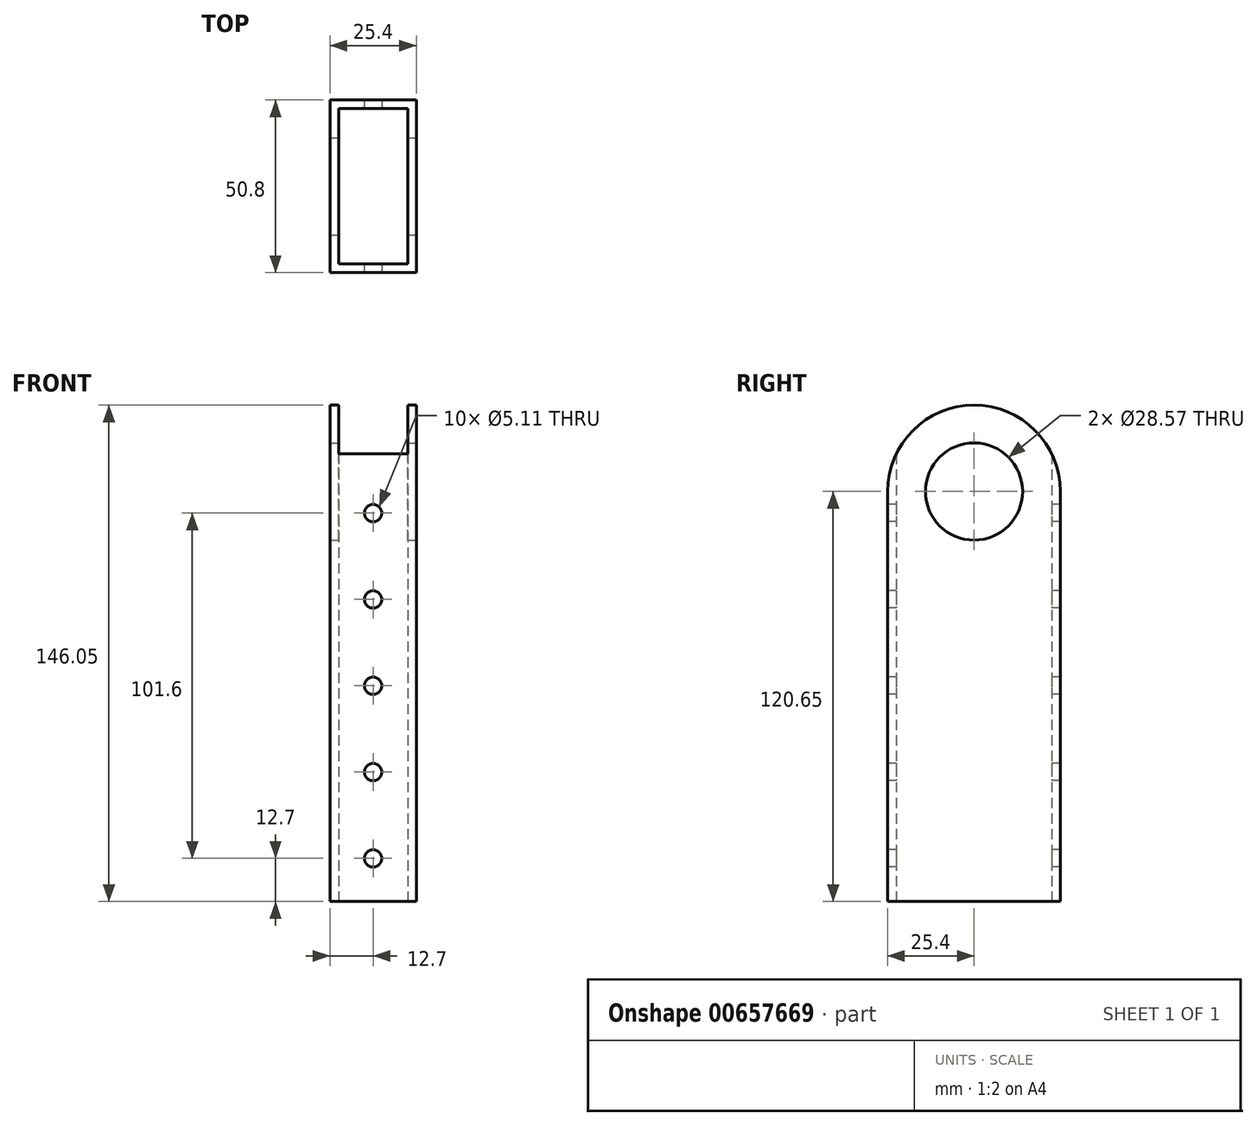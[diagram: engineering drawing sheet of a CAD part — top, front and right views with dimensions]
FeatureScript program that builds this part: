
annotation { "Feature Type Name" : "Feature", "Feature Type Description" : "" }
export const myFeature = defineFeature(function(context is Context, id is Id, definition is map)
    precondition{}
    {
        {
            var Q0;
            Q0=qCreatedBy(makeId("Top.planeOp"),FACE);
            var sketch = newSketch(context, id + "F0", { "sketchPlane" : qUnion([Q0])});
            skLineSegment(sketch, "E0.bottom", {"start": v(0, 0) * mm, "end": v(25.4, 0) * mm});
            skLineSegment(sketch, "E0.top", {"start": v(0, -50.8) * mm, "end": v(25.4, -50.8) * mm});
            skLineSegment(sketch, "E0.left", {"start": v(0, 0) * mm, "end": v(0, -50.8) * mm});
            skLineSegment(sketch, "E0.right", {"start": v(25.4, 0) * mm, "end": v(25.4, -50.8) * mm});
            skLineSegment(sketch, "E1.bottom", {"start": v(2.54, -2.54) * mm, "end": v(22.86, -2.54) * mm});
            skLineSegment(sketch, "E1.top", {"start": v(2.54, -48.26) * mm, "end": v(22.86, -48.26) * mm});
            skLineSegment(sketch, "E1.left", {"start": v(2.54, -2.54) * mm, "end": v(2.54, -48.26) * mm});
            skLineSegment(sketch, "E1.right", {"start": v(22.86, -2.54) * mm, "end": v(22.86, -48.26) * mm});
            skSolve(sketch);
        }
        {
            var Q0;
            Q0=makeQuery(id+"F0.imprint","IMPRINT",FACE,{"disambiguationData":[TD([[makeQuery(id+"F0.imprint","IMPRINT",EDGE,{"derivedFrom":sQuery(id+"F0.wireOp",EDGE,"E0.bottom")}),-1.0]])]});
            extrude(context, id + "F1", {"entities" : qUnion([Q0]), "depth" : 146.05 * mm, "offsetDistance" : 25.4 * mm});
        }
        {
            var Q0;
            Q0=makeQuery(id+"F1.opExtrude","SWEPT_FACE",FACE,{"disambiguationData":[OSD([sQuery(id+"F0.wireOp",EDGE,"E0.top")])]});
            var sketch = newSketch(context, id + "F2", { "sketchPlane" : qUnion([Q0])});
            skCircle(sketch, "E2", {"center": v(12.7, 12.7) * mm, "radius": 2.55 * mm});
            skCircle(sketch, "E3.0.1.0", {"center": v(12.7, 38.1) * mm, "radius": 2.55 * mm});
            skCircle(sketch, "E3.0.2.0", {"center": v(12.7, 63.5) * mm, "radius": 2.55 * mm});
            skCircle(sketch, "E3.0.3.0", {"center": v(12.7, 88.9) * mm, "radius": 2.55 * mm});
            skLineSegment(sketch, "E3.direction1", {"start": v(12.7, 12.7) * mm, "end": v(38.1, 12.7) * mm, "construction": true});
            skLineSegment(sketch, "E3.direction2", {"start": v(12.7, 12.7) * mm, "end": v(12.7, 38.1) * mm, "construction": true});
            skCircle(sketch, "E4.0.0.4", {"center": v(12.7, 114.3) * mm, "radius": 2.55 * mm});
            skCircle(sketch, "E4.0.0.5", {"center": v(12.7, 139.7) * mm, "radius": 2.55 * mm});
            skSolve(sketch);
        }
        {
            var Q0;
            Q0=makeQuery(id+"F2.imprint","IMPRINT",FACE,{"disambiguationData":[TD([[makeQuery(id+"F2.imprint","IMPRINT",EDGE,{"derivedFrom":sQuery(id+"F2.wireOp",EDGE,"E3.0.3.0")}),1.0]])]});
            var Q1;
            Q1=makeQuery(id+"F2.imprint","IMPRINT",FACE,{"disambiguationData":[TD([[makeQuery(id+"F2.imprint","IMPRINT",EDGE,{"derivedFrom":sQuery(id+"F2.wireOp",EDGE,"E3.0.2.0")}),1.0]])]});
            var Q2;
            Q2=makeQuery(id+"F2.imprint","IMPRINT",FACE,{"disambiguationData":[TD([[makeQuery(id+"F2.imprint","IMPRINT",EDGE,{"derivedFrom":sQuery(id+"F2.wireOp",EDGE,"E3.0.1.0")}),1.0]])]});
            var Q3;
            Q3=makeQuery(id+"F2.imprint","IMPRINT",FACE,{"disambiguationData":[TD([[makeQuery(id+"F2.imprint","IMPRINT",EDGE,{"derivedFrom":sQuery(id+"F2.wireOp",EDGE,"E2")}),1.0]])]});
            var Q4;
            Q4=makeQuery(id+"F2.imprint","IMPRINT",FACE,{"disambiguationData":[TD([[makeQuery(id+"F2.imprint","IMPRINT",EDGE,{"derivedFrom":sQuery(id+"F2.wireOp",EDGE,"E4.0.0.4")}),1.0]])]});
            var Q5;
            Q5=makeQuery(id+"F2.imprint","IMPRINT",FACE,{"disambiguationData":[TD([[makeQuery(id+"F2.imprint","IMPRINT",EDGE,{"derivedFrom":sQuery(id+"F2.wireOp",EDGE,"E4.0.0.5")}),1.0]])]});
            extrude(context, id + "F3", {"entities" : qUnion([Q0, Q1, Q2, Q3, Q4, Q5]), "operationType" : NewBodyOperationType.REMOVE, "oppositeDirection" : true, "depth" : 76.2 * mm, "offsetDistance" : 25.4 * mm});
        }
        {
            var Q0;
            Q0=makeQuery(id+"F1.opExtrude","SWEPT_FACE",FACE,{"disambiguationData":[OSD([sQuery(id+"F0.wireOp",EDGE,"E0.right")])]});
            var sketch = newSketch(context, id + "F4", { "sketchPlane" : qUnion([Q0])});
            skCircle(sketch, "E5", {"center": v(-27.23, 38.1) * mm, "radius": 63.5 * mm});
            skCircle(sketch, "E6", {"center": v(-25.4, 120.65) * mm, "radius": 14.29 * mm});
            skCircle(sketch, "E7", {"center": v(-25.4, 120.65) * mm, "radius": 25.4 * mm});
            skLineSegment(sketch, "E8", {"start": v(0, -12.7) * mm, "end": v(-89.8, 77.1) * mm});
            skLineSegment(sketch, "E9", {"start": v(-44.45, 19.18) * mm, "end": v(-39.96, 14.69) * mm});
            skLineSegment(sketch, "E10", {"start": v(-39.96, 14.69) * mm, "end": v(-33.67, 20.97) * mm});
            skSolve(sketch);
        }
        {
            var Q0;
            Q0=makeQuery(id+"F4.imprint","IMPRINT",FACE,{"disambiguationData":[TD([[makeQuery(id+"F4.imprint","IMPRINT",EDGE,{"derivedFrom":sQuery(id+"F4.wireOp",EDGE,"E6")}),1.0]])]});
            var Q1;
            {var subQ0=sQuery(id+"F4.wireOp",EDGE,"jfRsKdR6-lV6r-LF2K-yryt-jh4fqjNjW3CK");var subQ1=sQuery(id+"F4.wireOp",EDGE,"XPiz7BX0-e647-BFaL-DDcZ-xSguP5itvhAC");var subQ2=makeQuery(id+"F4.imprint","INTERSECT",VERTEX,{"derivedFrom":[subQ1,subQ0]});Q1=makeQuery(id+"F4.imprint","IMPRINT",FACE,{"disambiguationData":[TD([[makeQuery(id+"F4.imprint","IMPRINT",EDGE,{"disambiguationData":[TD([[subQ2,-1.0]])],"derivedFrom":subQ1}),1.0]])]});}
            var Q2;
            {var subQ0=sQuery(id+"F4.wireOp",EDGE,"0JtLs2co-jAV2-Ispk-Zqz6-pszSj5jpMm16");var subQ1=sQuery(id+"F4.wireOp",EDGE,"XPiz7BX0-e647-BFaL-DDcZ-xSguP5itvhAC");var subQ2=makeQuery(id+"F4.imprint","INTERSECT",VERTEX,{"derivedFrom":[subQ1,subQ0]});Q2=makeQuery(id+"F4.imprint","IMPRINT",FACE,{"disambiguationData":[TD([[makeQuery(id+"F4.imprint","IMPRINT",EDGE,{"disambiguationData":[TD([[subQ2,1.0]])],"derivedFrom":subQ1}),1.0]])]});}
            var Q3;
            {var subQ0=sQuery(id+"F4.wireOp",EDGE,"jfRsKdR6-lV6r-LF2K-yryt-jh4fqjNjW3CK");var subQ1=sQuery(id+"F4.wireOp",EDGE,"XPiz7BX0-e647-BFaL-DDcZ-xSguP5itvhAC");var subQ2=makeQuery(id+"F4.imprint","INTERSECT",VERTEX,{"derivedFrom":[subQ1,subQ0]});Q3=makeQuery(id+"F4.imprint","IMPRINT",FACE,{"disambiguationData":[TD([[makeQuery(id+"F4.imprint","IMPRINT",EDGE,{"disambiguationData":[TD([[subQ2,1.0]])],"derivedFrom":subQ1}),1.0]])]});}
            var Q4;
            {var subQ0=sQuery(id+"F4.wireOp",EDGE,"FucTxrkd-sa56-i95p-2rhM-JDqMKA7fs8Ty");var subQ1=sQuery(id+"F4.wireOp",EDGE,"5fbN0qHQ-40By-CurH-I46S-oSeFOKhkzDAV");var subQ2=makeQuery(id+"F4.imprint","INTERSECT",VERTEX,{"derivedFrom":[subQ1,subQ0]});Q4=makeQuery(id+"F4.imprint","IMPRINT",FACE,{"disambiguationData":[TD([[makeQuery(id+"F4.imprint","IMPRINT",EDGE,{"disambiguationData":[TD([[subQ2,1.0]])],"derivedFrom":subQ1}),1.0]])]});}
            var Q5;
            {var subQ0=sQuery(id+"F4.wireOp",EDGE,"FucTxrkd-sa56-i95p-2rhM-JDqMKA7fs8Ty");var subQ1=sQuery(id+"F4.wireOp",EDGE,"5fbN0qHQ-40By-CurH-I46S-oSeFOKhkzDAV");var subQ2=makeQuery(id+"F4.imprint","INTERSECT",VERTEX,{"derivedFrom":[subQ1,subQ0]});Q5=makeQuery(id+"F4.imprint","IMPRINT",FACE,{"disambiguationData":[TD([[makeQuery(id+"F4.imprint","IMPRINT",EDGE,{"disambiguationData":[TD([[subQ2,-1.0]])],"derivedFrom":subQ1}),1.0]])]});}
            var Q6;
            {var subQ0=sQuery(id+"F4.wireOp",EDGE,"5fbN0qHQ-40By-CurH-I46S-oSeFOKhkzDAV");var subQ1=makeQuery(id+"F4.imprint","INTERSECT",VERTEX,{"derivedFrom":[subQ0,sQuery(id+"F4.wireOp",EDGE,"FucTxrkd-sa56-i95p-2rhM-JDqMKA7fs8Ty")]});Q6=makeQuery(id+"F4.imprint","IMPRINT",FACE,{"disambiguationData":[TD([[makeQuery(id+"F4.imprint","IMPRINT",EDGE,{"disambiguationData":[TD([[subQ1,1.0]])],"derivedFrom":subQ0}),-1.0]])]});}
            var Q7;
            {var subQ0=sQuery(id+"F4.wireOp",EDGE,"5fbN0qHQ-40By-CurH-I46S-oSeFOKhkzDAV");var subQ1=makeQuery(id+"F4.imprint","INTERSECT",VERTEX,{"derivedFrom":[subQ0,sQuery(id+"F4.wireOp",EDGE,"jfRsKdR6-lV6r-LF2K-yryt-jh4fqjNjW3CK")]});Q7=makeQuery(id+"F4.imprint","IMPRINT",FACE,{"disambiguationData":[TD([[makeQuery(id+"F4.imprint","IMPRINT",EDGE,{"disambiguationData":[TD([[subQ1,1.0]])],"derivedFrom":subQ0}),-1.0]])]});}
            var Q8;
            {var subQ0=sQuery(id+"F4.wireOp",EDGE,"jfRsKdR6-lV6r-LF2K-yryt-jh4fqjNjW3CK");var subQ1=sQuery(id+"F4.wireOp",EDGE,"5fbN0qHQ-40By-CurH-I46S-oSeFOKhkzDAV");var subQ2=makeQuery(id+"F4.imprint","INTERSECT",VERTEX,{"derivedFrom":[subQ1,subQ0]});Q8=makeQuery(id+"F4.imprint","IMPRINT",FACE,{"disambiguationData":[TD([[makeQuery(id+"F4.imprint","IMPRINT",EDGE,{"disambiguationData":[TD([[subQ2,-1.0]])],"derivedFrom":subQ1}),1.0]])]});}
            var Q9;
            {var subQ0=sQuery(id+"F4.wireOp",EDGE,"jfRsKdR6-lV6r-LF2K-yryt-jh4fqjNjW3CK");var subQ1=sQuery(id+"F4.wireOp",EDGE,"5fbN0qHQ-40By-CurH-I46S-oSeFOKhkzDAV");var subQ2=makeQuery(id+"F4.imprint","INTERSECT",VERTEX,{"derivedFrom":[subQ1,subQ0]});Q9=makeQuery(id+"F4.imprint","IMPRINT",FACE,{"disambiguationData":[TD([[makeQuery(id+"F4.imprint","IMPRINT",EDGE,{"disambiguationData":[TD([[subQ2,1.0]])],"derivedFrom":subQ1}),1.0]])]});}
            var Q10;
            {var subQ0=sQuery(id+"F4.wireOp",EDGE,"E7");var subQ1=sQuery(id+"F0.wireOp",EDGE,"E0.right");var subQ2=makeQuery(id+"F1.opExtrude","CAP_EDGE",EDGE,{"disambiguationData":[OSD([subQ1])],"isStart":false});var subQ3=makeQuery(id+"F4.imprint","INTERSECT",VERTEX,{"derivedFrom":[subQ2,subQ0]});Q10=makeQuery(id+"F4.imprint","IMPRINT",FACE,{"disambiguationData":[TD([[makeQuery(id+"F4.imprint","IMPRINT",EDGE,{"disambiguationData":[TD([[subQ3,-1.0]])],"derivedFrom":subQ0}),-1.0]])]});}
            var Q11;
            {var subQ0=sQuery(id+"F4.wireOp",EDGE,"E7");var subQ1=sQuery(id+"F0.wireOp",EDGE,"E0.right");var subQ2=makeQuery(id+"F1.opExtrude","CAP_EDGE",EDGE,{"disambiguationData":[OSD([subQ1])],"isStart":false});var subQ3=makeQuery(id+"F4.imprint","INTERSECT",VERTEX,{"derivedFrom":[subQ2,subQ0]});Q11=makeQuery(id+"F4.imprint","IMPRINT",FACE,{"disambiguationData":[TD([[makeQuery(id+"F4.imprint","IMPRINT",EDGE,{"disambiguationData":[TD([[subQ3,1.0]])],"derivedFrom":subQ0}),-1.0]])]});}
            var Q12;
            Q12=makeQuery(id+"F4.imprint","IMPRINT",FACE,{"disambiguationData":[TD([[makeQuery(id+"F4.imprint","IMPRINT",EDGE,{"derivedFrom":sQuery(id+"F4.wireOp",EDGE,"wRuUoUPN-ylMf-ALfK-cmLu-fabLM8s5z77o")}),1.0]])]});
            var Q13;
            Q13=makeQuery(id+"F4.imprint","IMPRINT",FACE,{"disambiguationData":[TD([[makeQuery(id+"F4.imprint","IMPRINT",EDGE,{"derivedFrom":sQuery(id+"F4.wireOp",EDGE,"UfALe54z-BqD8-81Vj-kJDC-khd1eAjdLLJo")}),1.0]])]});
            extrude(context, id + "F5", {"entities" : qUnion([Q0, Q1, Q2, Q3, Q4, Q5, Q6, Q7, Q8, Q9, Q10, Q11, Q12, Q13]), "operationType" : NewBodyOperationType.REMOVE, "oppositeDirection" : true, "depth" : 25.4 * mm, "offsetDistance" : 25.4 * mm});
        }
    });
